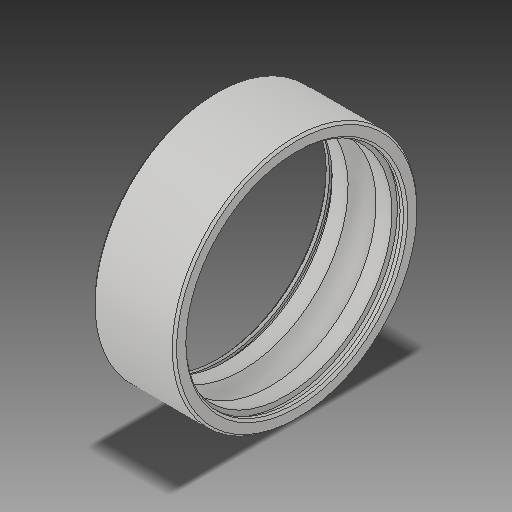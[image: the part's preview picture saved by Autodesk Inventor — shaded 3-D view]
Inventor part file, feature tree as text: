
AUTODESK INVENTOR PART (.ipt)
format: ipt  version: 2017.3 (Build 213256000, 256)  size: 178,176 bytes
history: mixed  units: mm
features: chamfer x1, imported_body x1
ambient origin geometry x8: Origin, YZ Plane, XZ Plane, XY Plane, X Axis, Y Axis, Z Axis, Center Point
bodies: Solid1 (imported_parasolid)
feature tree (2):
  chamfer  "Chamfer1"  [1 undecoded]
  imported_body  NMx_Import_Brep_tag  [imported B-rep: ~18 faces, bbox_mm=[3.0, 9.0, 0.0]]
note: 1 required parameter value undecoded (feature->parameter linkage not recoverable at this tier; creation-order binding heuristic only, values carry confidence <= 0.55)
